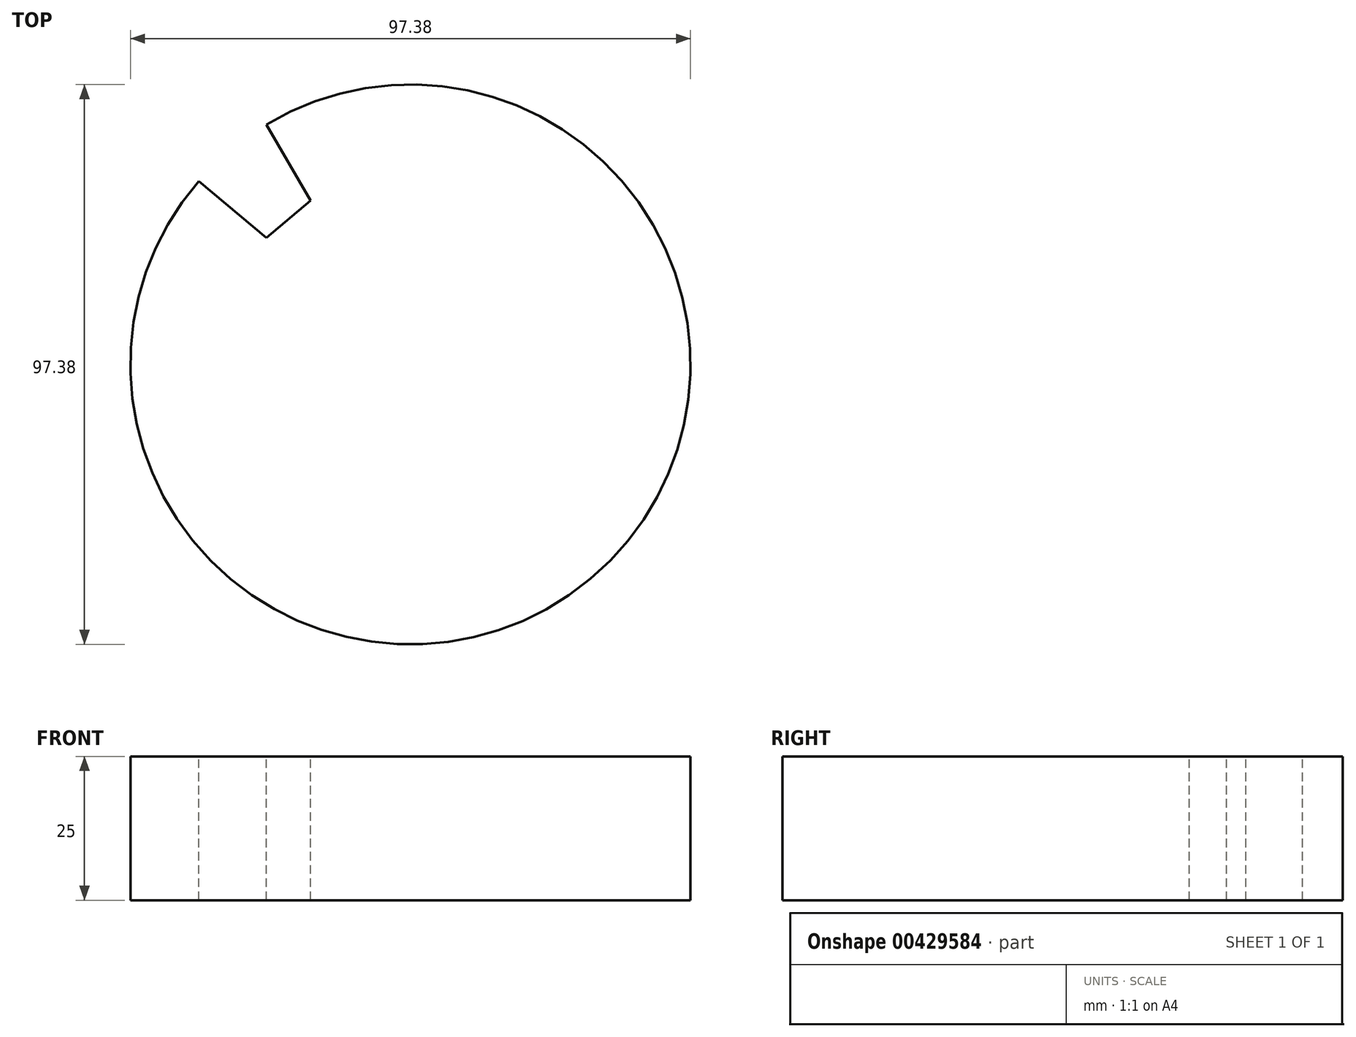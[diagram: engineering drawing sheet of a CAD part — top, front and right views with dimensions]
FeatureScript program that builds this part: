
annotation { "Feature Type Name" : "Feature", "Feature Type Description" : "" }
export const myFeature = defineFeature(function(context is Context, id is Id, definition is map)
    precondition{}
    {
        {
            var Q0;
            Q0=qCreatedBy(makeId("Top.planeOp"),FACE);
            var sketch = newSketch(context, id + "F0", { "sketchPlane" : qUnion([Q0])});
            skCircle(sketch, "E0", {"center": v(0, 0) * mm, "radius": 48.69 * mm});
            skSolve(sketch);
        }
        {
            var Q0;
            Q0=makeQuery(id+"F0.imprint","IMPRINT",FACE,{"disambiguationData":[TD([[makeQuery(id+"F0.imprint","IMPRINT",EDGE,{"derivedFrom":sQuery(id+"F0.wireOp",EDGE,"E0")}),1.0]])]});
            extrude(context, id + "F1", {"entities" : qUnion([Q0]), "depth" : 25 * mm});
        }
        {
            var Q0;
            Q0=makeQuery(id+"F1.opExtrude","CAP_FACE",FACE,{"disambiguationData":[OSD([sQuery(id+"F0.wireOp",EDGE,"E0")])],"isStart":false});
            var sketch = newSketch(context, id + "F2", { "sketchPlane" : qUnion([Q0])});
            skLineSegment(sketch, "E1", {"start": v(-48.66, 58) * mm, "end": v(0, 0) * mm, "construction": true});
            skLineSegment(sketch, "E2", {"start": v(-33.22, 55.92) * mm, "end": v(-49.3, 42.42) * mm});
            skLineSegment(sketch, "E3", {"start": v(-49.3, 42.42) * mm, "end": v(-25.04, 22.07) * mm});
            skLineSegment(sketch, "E4", {"start": v(-25.04, 22.07) * mm, "end": v(-17.38, 28.5) * mm});
            skLineSegment(sketch, "E5", {"start": v(-17.38, 28.5) * mm, "end": v(-33.22, 55.92) * mm});
            skSolve(sketch);
        }
        {
            var Q0;
            {var subQ0=sQuery(id+"F2.wireOp",EDGE,"E4");Q0=makeQuery(id+"F2.imprint","IMPRINT",FACE,{"disambiguationData":[TD([[makeQuery(id+"F2.imprint","IMPRINT",EDGE,{"derivedFrom":subQ0}),1.0]])]});}
            extrude(context, id + "F3", {"entities" : qUnion([Q0]), "operationType" : NewBodyOperationType.REMOVE, "endBound" : BoundingType.THROUGH_ALL, "oppositeDirection" : true, "depth" : 25 * mm});
        }
    });
